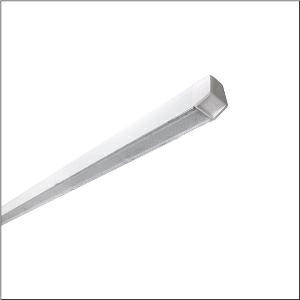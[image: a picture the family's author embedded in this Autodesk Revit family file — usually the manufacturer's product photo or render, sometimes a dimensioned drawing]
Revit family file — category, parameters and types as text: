
# Revit family: licross_r__11_recessed_ho_51ul1edv4m5r00s_7b8d
name_source: partatom
category: Lighting Fixtures
units: mm (PartAtom-declared; Revit-internal decimal feet)

## family parameters
Cut with Voids When Loaded = No
Host = Face
Light Source = No
Part Type = Normal
Room Calculation Point = No
Round Connector Dimension = Use Diameter
Shared = No

## types (1)
- --- (1 x LED, 25560 lm, 150.1 W, 4000K)
    Apparent Load = 150 VA
    CIE Flux Codes = 85 95 99 100 100
    Color Rendering = 80
    Color Temperature = 4000K
    Default Elevation = 1800 mm
    Description = Licross® 11 Recessed HO, single luminaire, primary optical cover: cover, of PMMA, light emission: direct distribution, primary light characteristic: symmetric, installation type: slip-in mounting, LED, rated luminous flux: 25.560lm, luminous efficacy: 170lm/W, light colour: 840, colour temperature: 4000K, control gear: ECG DALI, with terminal, 5-pole, max. 2.5mm², mains connection: 230V, AC, 50/60Hz, rated input power: 150W, Licross® LED insert, of sheet steel, galvanised, coil coated, white, with terminals, length: 2.327mm, width: 70mm, height: 71mm, end cap, of PC, white, mounting rail, of sheet steel, galvanised, white, protection rating (complete): IP20, insulation class (complete): insulation class I (protective earthing), certification: CE, ENEC, VDE, UKCA, impact resistance: IK06, permissible operating ambient temperature: -35..+35°C, corresponds to IFS (International Featured Standards) requirements for safety and quality in the food industry, reducing of maximum allowable ambient temperature of 5°C with ceiling mounting, LABS conformity tested according to VDMA 24364:2018-05, packaging unit: 1 piece
    Height = 58 mm
    Lamp = 1 x LED
    Lamp Light Flux = 25560 lm
    Lamp Power = 150.1 W
    Lamp count = 1
    Length = 2250 mm
    Luminous efficacy = 170 lm/W
    Manufacturer = Siteco
    ModVariant = No
    Model = 51UL1EDV4M5R00S
    Mounting Place = Ceiling
    Mounting Type = Pendant
    Number of Poles = 1
    OnlyDefault = Yes
    Power Factor = 1
    Product Name = Licross® 11 Recessed HO
    Product group = single luminaire
    ProductGroupID = 907
    Protection Class = Protection class I
    Protection Degree = IP 20
    RLX_Detail_Level = 1
    RLX_Emergency_Light_Flux = 0 lm
    RLX_Emergency_Type = 0
    RLX_Emergency_Type_DB = No
    RlxData = <blob elided: 32061 chars, md5=4de9a8b5>
    Socket = socket
    Standby Power = 0 W
    System Light Flux = 25561 lm
    System Power = 150 W
    Type Comments = factory setting: luminous flux: 100 % | dim-lin: 254 | 575 mA
    Type Image = l_1006979.jpg
    URL = http://relux.com
    VarID = @adj_112565
    Voltage = 0 V
    Weight = 0.00 kg
    Width = 66 mm

## geometry (parser evidence)
native form markers: Blend x4, Sweep x8
no freeform markers — native parametric forms only
